# Revit family: Ladder_Rung_Kattsafe_Vertical_Caged
name_source: partatom
category: Specialty Equipment
units: mm (PartAtom-declared; Revit-internal decimal feet)

## family parameters
Always vertical = Yes
Cut with Voids When Loaded = No
Enable Cutting in Views = No
Maintain Annotation Orientation = No
OmniClass Number = 23.17.23.15
Part Type = Normal
Room Calculation Point = No
Round Connector Dimension = Use Diameter
Shared = No
Work Plane-Based = No

## types (2) — shared parameters
Angle = 90.00°
Assembly Code = E1090100
ElementType = Ladder
Export Type to IFC As = IfcBuildingElementProxy
IfcExportAs = IfcBuildingElementProxy
IfcExportType = USERDEFINED
Manufacturer = Kattsafe®
ManufacturerURLProductSpecific = https://kattsafe.com.au
Material = Aluminum_Kattsafe_Satin
ModifiedIssue = 20250224 $
Type Comments = Ladder - Vertical - Rung - Caged
Type IFC Predefined Type = USERDEFINED
URL = https://kattsafe.com.au
Uniclass2015Code = Pr_25_30_85_02
Uniclass2015Title = Access ladders
Uniclass2015Version = Products v1.35
zero-valued in all types: Default Elevation

## per-type parameters (varying)
| type | DRail | Description | Guardrail | ManufacturerOverallWidth | ManufacturerSpecCode | Model |
| Guardrail (RL41) | No | Vertical caged ladder with guardrails and 1.0m landing. Available with metal deck and concrete floor mounting options | Yes | 1400 mm  [stored 4.59318 ft] | RL41 | RL41 |
| D-Rail (RL41D) | Yes | Vertical caged ladder with d-rails and 1.0m landing. Available with metal deck and concrete floor mounting options | No | 800 mm  [stored 2.62467 ft] | RL41D | RL41D |

note: [stored X ft] marks values corroborated as IEEE doubles in the binary element streams (Revit-internal decimal feet)

## geometry (parser evidence)
native form markers: Sweep x17
no freeform markers — native parametric forms only
